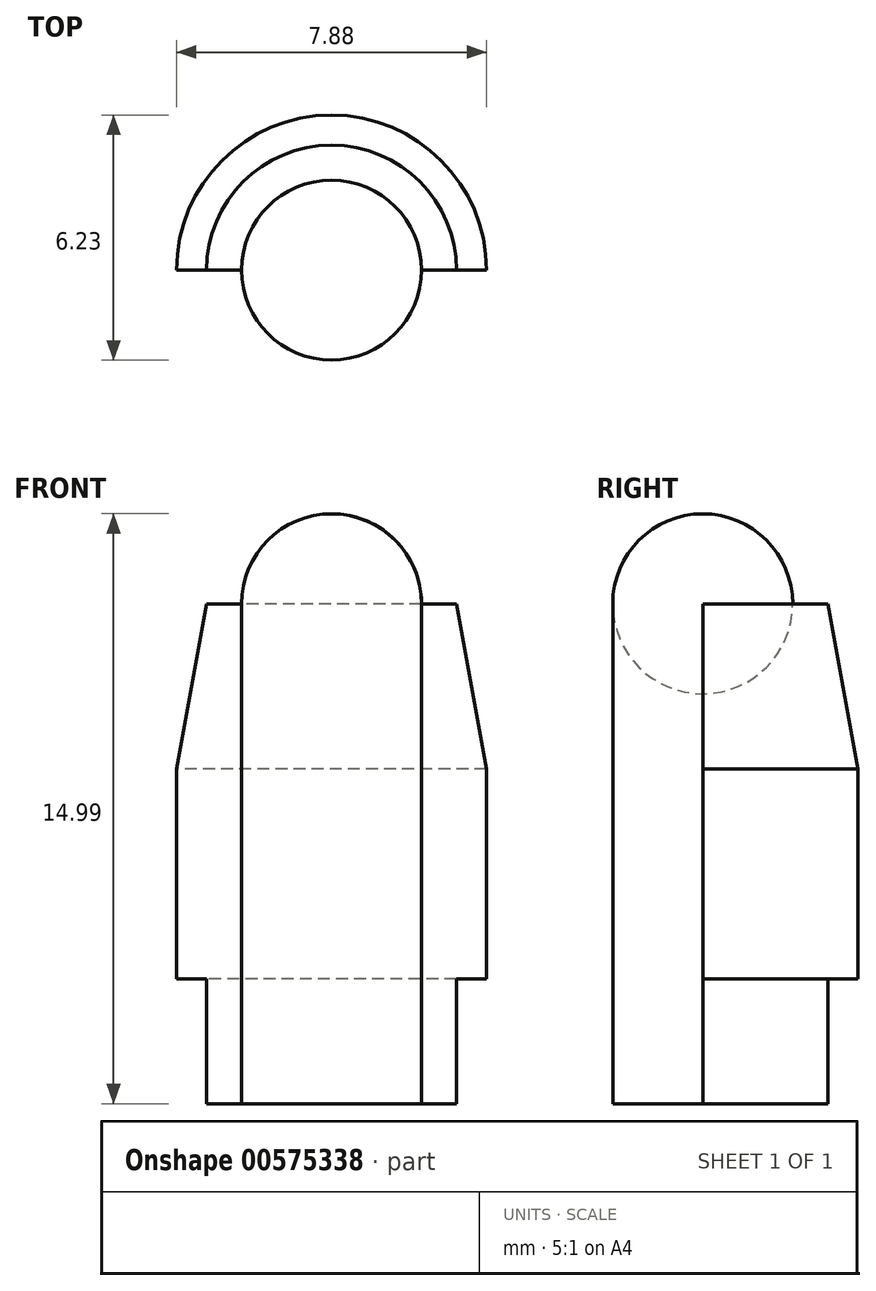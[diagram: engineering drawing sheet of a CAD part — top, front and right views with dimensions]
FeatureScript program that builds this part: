
annotation { "Feature Type Name" : "Feature", "Feature Type Description" : "" }
export const myFeature = defineFeature(function(context is Context, id is Id, definition is map)
    precondition{}
    {
        {
            var Q0;
            Q0=qCreatedBy(makeId("Front.planeOp"),FACE);
            var sketch = newSketch(context, id + "F0", { "sketchPlane" : qUnion([Q0])});
            skLineSegment(sketch, "E0", {"start": v(-2.29, 8.13) * mm, "end": v(-2.29, -4.57) * mm});
            skLineSegment(sketch, "E1", {"start": v(-2.29, -4.57) * mm, "end": v(0, -4.57) * mm});
            skLineSegment(sketch, "E2", {"start": v(0, -4.57) * mm, "end": v(-3.18, -4.57) * mm});
            skLineSegment(sketch, "E3", {"start": v(-3.18, -4.57) * mm, "end": v(-3.18, -1.4) * mm});
            skLineSegment(sketch, "E4", {"start": v(-3.94, -1.4) * mm, "end": v(-3.94, 3.94) * mm});
            skLineSegment(sketch, "E5", {"start": v(-3.17, 8.13) * mm, "end": v(-3.94, 3.94) * mm});
            skLineSegment(sketch, "E6", {"start": v(-3.17, 8.13) * mm, "end": v(-2.29, 8.13) * mm});
            skLineSegment(sketch, "E7", {"start": v(-3.94, -1.4) * mm, "end": v(-3.18, -1.4) * mm});
            skArc(sketch, "E8", {"start": v(-2.29, 8.13) * mm, "mid": v(-1.62, 9.75) * mm, "end": v(0, 10.42) * mm});
            skLineSegment(sketch, "E9", {"start": v(0, 10.42) * mm, "end": v(0, -4.57) * mm});
            skLineSegment(sketch, "E10", {"start": v(0, 11.8) * mm, "end": v(0, -6.41) * mm, "construction": true});
            skSolve(sketch);
        }
        {
            var Q0;
            {var subQ0=sQuery(id+"F0.wireOp",EDGE,"E0");Q0=makeQuery(id+"F0.imprint","IMPRINT",FACE,{"disambiguationData":[TD([[makeQuery(id+"F0.imprint","IMPRINT",EDGE,{"derivedFrom":subQ0}),1.0]])]});}
            var Q1;
            Q1=sQuery(id+"F0.wireOp",EDGE,"E10");
            revolve(context, id + "F1", {"entities" : qUnion([Q0]), "axis" : qUnion([Q1]), "revolveType" : RevolveType.FULL});
        }
        {
            var Q0;
            {var subQ2=sQuery(id+"F0.wireOp",EDGE,"E0");Q0=makeQuery(id+"F0.imprint","IMPRINT",FACE,{"disambiguationData":[TD([[makeQuery(id+"F0.imprint","IMPRINT",EDGE,{"derivedFrom":subQ2}),-1.0]])]});}
            var Q1;
            Q1=sQuery(id+"F0.wireOp",EDGE,"E10");
            revolve(context, id + "F2", {"operationType" : NewBodyOperationType.ADD, "entities" : qUnion([Q0]), "axis" : qUnion([Q1]), "revolveType" : RevolveType.ONE_DIRECTION, "angle" : 180 * degree});
        }
    });
